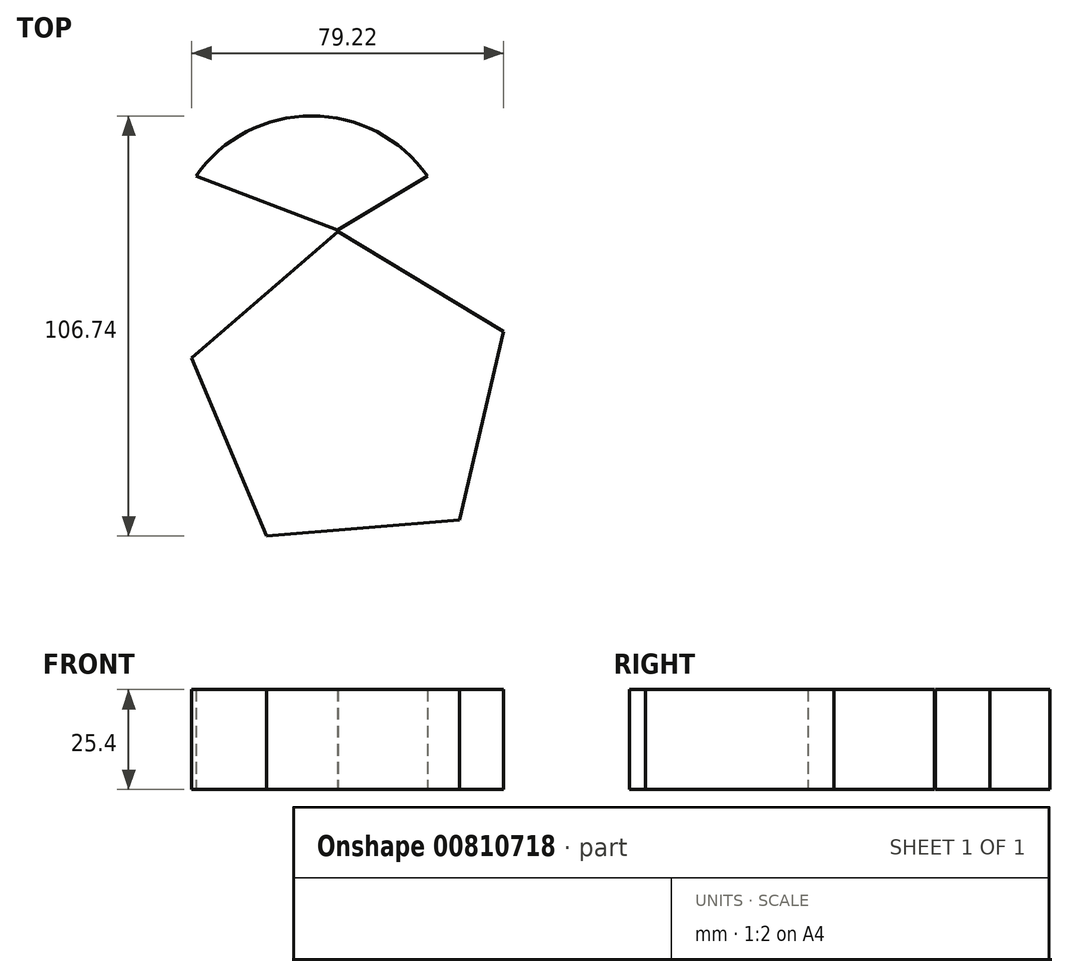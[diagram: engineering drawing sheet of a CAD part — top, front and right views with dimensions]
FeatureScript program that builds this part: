
annotation { "Feature Type Name" : "Feature", "Feature Type Description" : "" }
export const myFeature = defineFeature(function(context is Context, id is Id, definition is map)
    precondition{}
    {
        {
            var Q0;
            Q0=qCreatedBy(makeId("Top.planeOp"),FACE);
            var sketch = newSketch(context, id + "F0", { "sketchPlane" : qUnion([Q0])});
            skCircle(sketch, "E0.cCircle", {"center": v(0, 0) * mm, "radius": 33.82 * mm, "construction": true});
            skLineSegment(sketch, "E0.0", {"start": v(-40.7, 9.55) * mm, "end": v(-3.5, 41.65) * mm});
            skLineSegment(sketch, "E0.1", {"start": v(-3.5, 41.65) * mm, "end": v(38.53, 16.2) * mm});
            skLineSegment(sketch, "E0.2", {"start": v(38.53, 16.2) * mm, "end": v(27.31, -31.64) * mm});
            skLineSegment(sketch, "E0.3", {"start": v(27.31, -31.64) * mm, "end": v(-21.65, -35.75) * mm});
            skLineSegment(sketch, "E0.4", {"start": v(-21.65, -35.75) * mm, "end": v(-40.7, 9.55) * mm});
            skPoint(sketch, "E0.0.midPoint", {"position": v(-22.1, 25.6) * mm});
            skSolve(sketch);
        }
        {
            var Q0;
            Q0=qCreatedBy(makeId("Top.planeOp"),FACE);
            var sketch = newSketch(context, id + "F1", { "sketchPlane" : qUnion([Q0])});
            skLineSegment(sketch, "E1", {"start": v(-40.78, 10.03) * mm, "end": v(-39.62, 55.77) * mm});
            skLineSegment(sketch, "E2", {"start": v(-3.6, 41.95) * mm, "end": v(-39.62, 55.77) * mm});
            skLineSegment(sketch, "E3", {"start": v(-3.6, 41.95) * mm, "end": v(19.18, 55.77) * mm});
            skArc(sketch, "E4", {"start": v(19.18, 55.77) * mm, "mid": v(-10.22, 70.99) * mm, "end": v(-39.62, 55.77) * mm});
            skLineSegment(sketch, "E5", {"start": v(19.18, 55.77) * mm, "end": v(38.45, 16.45) * mm});
            skSolve(sketch);
        }
        {
            var Q0;
            Q0=makeQuery(id+"F0.imprint","IMPRINT",FACE,{"disambiguationData":[TD([[makeQuery(id+"F0.imprint","IMPRINT",EDGE,{"derivedFrom":sQuery(id+"F0.wireOp",EDGE,"E0.0")}),-1.0]])]});
            var Q1;
            Q1=makeQuery(id+"F1.imprint","IMPRINT",FACE,{"disambiguationData":[TD([[makeQuery(id+"F1.imprint","IMPRINT",EDGE,{"derivedFrom":sQuery(id+"F1.wireOp",EDGE,"E2")}),-1.0]])]});
            extrude(context, id + "F2", {"entities" : qUnion([Q0, Q1]), "depth" : 25.4 * mm, "offsetDistance" : 25.4 * mm});
        }
    });
